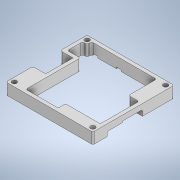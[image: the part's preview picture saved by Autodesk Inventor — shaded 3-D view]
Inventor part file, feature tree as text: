
AUTODESK INVENTOR PART (.ipt)
format: ipt  version: 2020.3 (Build 243373000, 373)  size: 268,288 bytes
history: native  units: in
note: dims shown in document units (in); Inventor stores cm internally (conversion verified against a paired STEP export)
features: fillet x4, extrude x3, sketch x3, direct_edit x1, move_body x1
ambient origin geometry x8: Origin, YZ Plane, XZ Plane, XY Plane, X Axis, Y Axis, Z Axis, Center Point
bodies: Solid1 (feature_tree)
feature tree (12):
  extrude  "Extrusion1"  Depth=1.74in
  extrude  "Extrusion2"  Depth=0.575in
  extrude  "Extrusion3"  Depth=0.0138in
  direct_edit  "Direct Edit1"
  fillet  "Fillet1"  Radius=0.1725in
  fillet  "Fillet3"  Radius=0.1725in
  fillet  "Fillet4"  Radius=0.1725in
  fillet  "Fillet5"  Radius=0.1725in
  sketch  "Sketch1"  dims[d0=1.8625in d1=1.74in]
  sketch  "Sketch2"  dims[d2=0.575in d3=0.575in]
  sketch  "Sketch3"  dims[d4=0.275in d5=0.1725in d6=0.1725in d7=0.1725in d8=0.1725in d9=0.1725in d10=0.1725in d11=0.1725in d12=0.1725in d13=0.1in d14=0.1in d15=0.1in d16=0.1in d17=0.09in d18=0.09in d19=0.09in d20=0.09in d21=0.09in d22=0.09in d23=0.09in d24=0.09in d25=0.075in d26=0.075in d27=0.075in d28=0.075in d29=0.237in d30=0.0in d31=0.43in d32=0.125in d33=0.677in d34=0.3275in d35=0.0955in d36=1.0in d37=0.0in d38=0.105in d39=0.033in d40=0.105in d41=0.033in d42=0.201in d43=1.0575in d44=1.0in d45=0.0in d46=0.2345in d47=0.82in d48=0.6725in d49=0.3in d50=0.0in d51=0.0in d52=0.0045in d53=0.0375in d55=0.0138in d56=0.0375in d57=0.0138in]
  move_body  "Move1"
